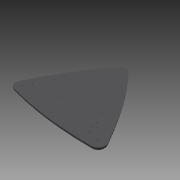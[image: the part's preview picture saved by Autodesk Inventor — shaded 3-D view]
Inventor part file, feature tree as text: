
AUTODESK INVENTOR PART (.ipt)
format: ipt  version: 2013 (Build 170138000, 138)  size: 201,216 bytes
history: native  units: mm
features: extrude x9, sketch x9, projected_geometry x4, fillet x2, reference x2, pattern_circular x1
ambient origin geometry x8: Origin, YZ Plane, XZ Plane, XY Plane, X Axis, Y Axis, Z Axis, Center Point
feature tree (27):
  extrude  "Extrusion2"  Depth=250.0mm
  extrude  "Extrusion9"  Depth=8.5mm
  pattern_circular  "Circular Pattern1"  Count=5  [1 undecoded]
  extrude  "Extrusion10"  Depth=25.0mm
  fillet  "Fillet2"  Radius=3.175mm
  extrude  "Extrusion3"  Depth=210.0mm
  extrude  "Extrusion4"  Depth=75.0mm
  extrude  "Extrusion5"  Depth=5.715mm TaperAngle=0.0deg
  fillet  "Fillet1"  Radius=25.0mm
  extrude  "Extrusion6"  Depth=3.175mm
  extrude  "Extrusion7"  Depth=12.7mm TaperAngle=0.0deg
  extrude  "Extrusion8"  Depth=3.2mm
  sketch  "Sketch1"  dims[d0=300.0mm d1=250.0mm]
  sketch  "Sketch2"  dims[d2=3.175mm d3=8.5mm d4=50.0mm]
  sketch  "Sketch3"  dims[d5=60.325mm d6=25.0mm d9=3.175mm]
  sketch  "Sketch4"  dims[d10=12.5mm d11=0.0mm d12=210.0mm]
  sketch  "Sketch5"  dims[d14=1.905mm d15=0.0mm d16=75.0mm]
  sketch  "Sketch6"  dims[d18=62.5mm d19=5.715mm d20=0.0mm d21=25.0mm]
  projected_geometry  "Projected Loop1"
  projected_geometry  "Projected Loop2"
  projected_geometry  "Projected Loop3"
  sketch  "Sketch7"  dims[d23=5.715mm d24=0.0mm d25=3.175mm]
  projected_geometry  "Projected Loop4"
  sketch  "Sketch8"  dims[d26=558.8mm d27=101.6mm d28=0.0mm d29=0.0mm d30=12.7mm d31=0.0mm]
  sketch  "Sketch9"  dims[d32=12.7mm d33=0.0mm d34=3.2mm d36=31.0mm d37=10.0mm d38=0.0mm d39=30.0mm d40=360.0deg d42=10.0mm d43=0.0mm d44=6.35mm]
  reference  "Reference1"
  reference  "Reference2"
note: 1 required parameter value undecoded (feature->parameter linkage not recoverable at this tier; creation-order binding heuristic only, values carry confidence <= 0.55)
